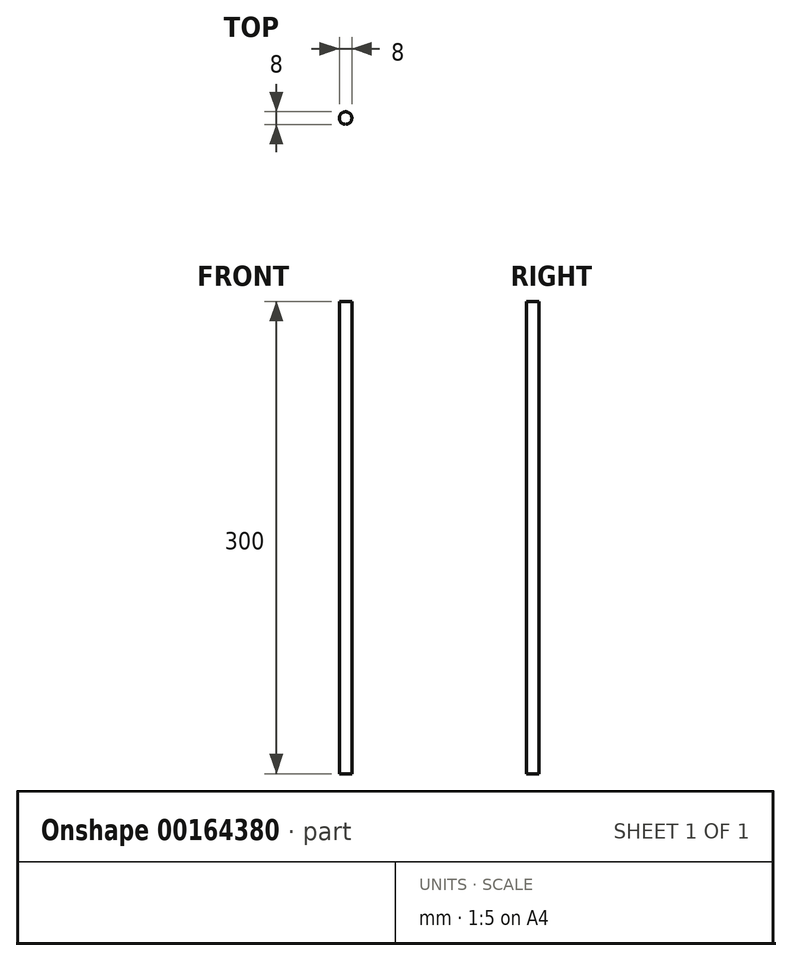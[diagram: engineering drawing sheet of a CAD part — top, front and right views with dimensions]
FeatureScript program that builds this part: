
annotation { "Feature Type Name" : "Feature", "Feature Type Description" : "" }
export const myFeature = defineFeature(function(context is Context, id is Id, definition is map)
    precondition{}
    {
        {
            var Q0;
            Q0=qCreatedBy(makeId("Top.planeOp"),FACE);
            var sketch = newSketch(context, id + "F0", { "sketchPlane" : qUnion([Q0])});
            skCircle(sketch, "E0", {"center": v(0, 0) * mm, "radius": 4 * mm});
            skSolve(sketch);
        }
        {
            var Q0;
            Q0 = qSketchRegion(id + "F0", true);
            extrude(context, id + "F1", {"entities" : qUnion([Q0]), "depth" : 300 * mm});
        }
    });
